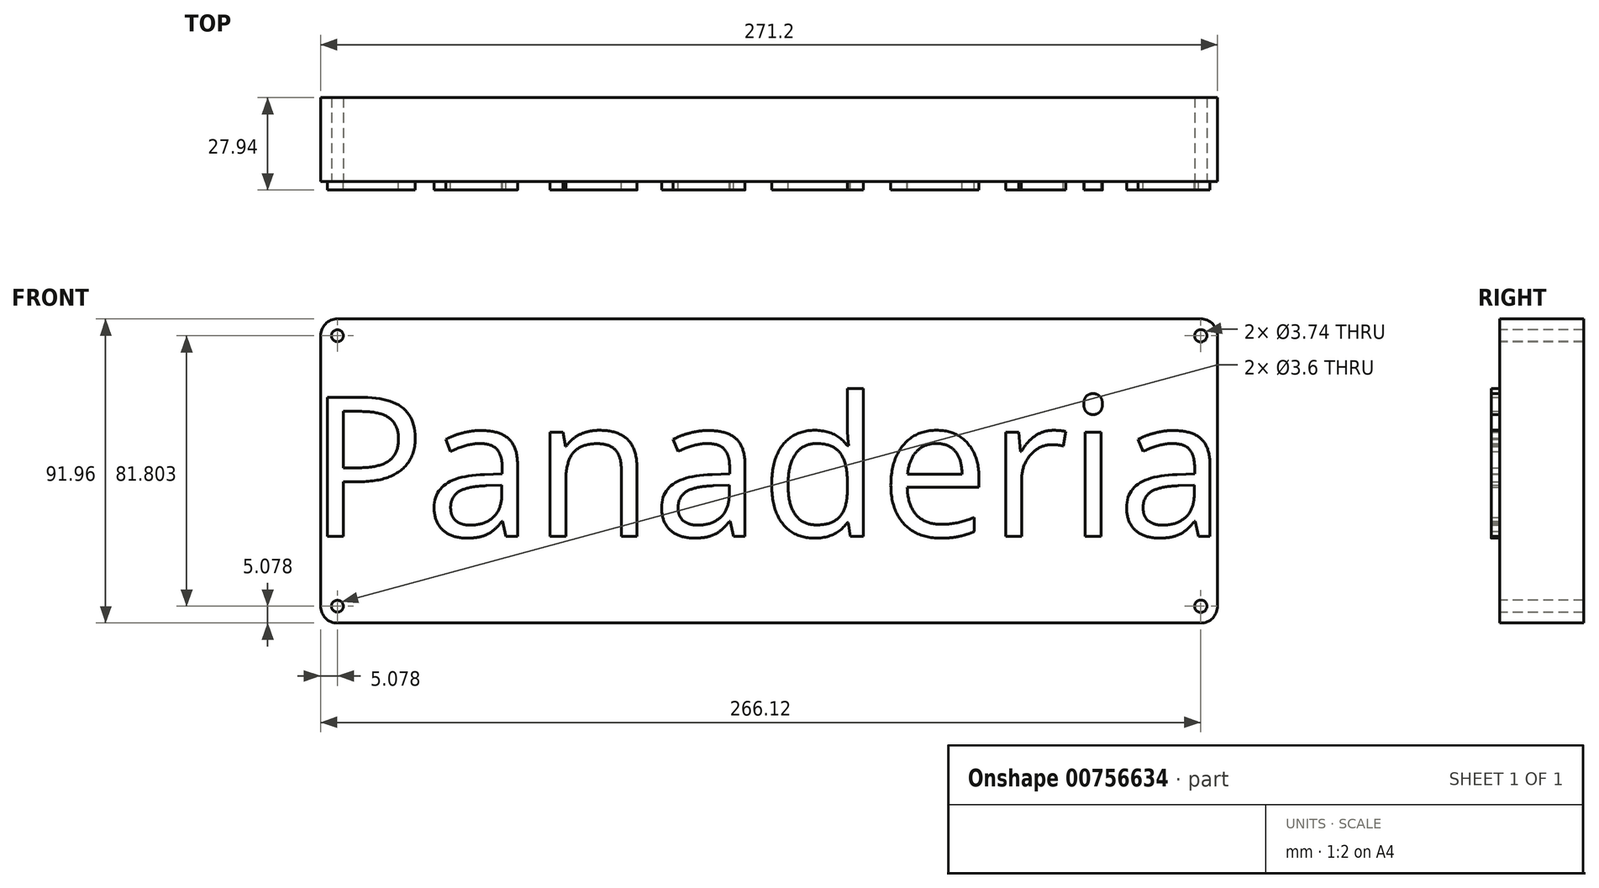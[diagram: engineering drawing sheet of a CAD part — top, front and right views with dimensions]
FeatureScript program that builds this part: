
annotation { "Feature Type Name" : "Feature", "Feature Type Description" : "" }
export const myFeature = defineFeature(function(context is Context, id is Id, definition is map)
    precondition{}
    {
        {
            var Q0;
            Q0=qCreatedBy(makeId("Front.planeOp"),FACE);
            var sketch = newSketch(context, id + "F0", { "sketchPlane" : qUnion([Q0])});
            skLineSegment(sketch, "E0.bottom", {"start": v(138.64, -45.98) * mm, "end": v(-132.56, -45.98) * mm});
            skLineSegment(sketch, "E0.top", {"start": v(138.64, 45.98) * mm, "end": v(-132.56, 45.98) * mm});
            skLineSegment(sketch, "E0.left", {"start": v(138.64, -45.98) * mm, "end": v(138.64, 45.98) * mm});
            skLineSegment(sketch, "E0.right", {"start": v(-132.56, -45.98) * mm, "end": v(-132.56, 45.98) * mm});
            skPoint(sketch, "E0.middle", {"position": v(3.04, 0) * mm});
            skSolve(sketch);
        }
        {
            var Q0;
            Q0=makeQuery(id+"F0.imprint","IMPRINT",FACE,{"disambiguationData":[TD([[makeQuery(id+"F0.imprint","IMPRINT",EDGE,{"derivedFrom":sQuery(id+"F0.wireOp",EDGE,"E0.bottom")}),-1.0]])]});
            extrude(context, id + "F1", {"entities" : qUnion([Q0]), "surfaceOperationType" : NewSurfaceOperationType.ADD, "depth" : 25.4 * mm, "offsetDistance" : 25.4 * mm});
        }
        {
            var Q0;
            Q0=makeQuery(id+"F1.opExtrude","CAP_FACE",FACE,{"disambiguationData":[OSD([sQuery(id+"F0.wireOp",EDGE,"E0.bottom"),sQuery(id+"F0.wireOp",EDGE,"E0.top"),sQuery(id+"F0.wireOp",EDGE,"E0.left"),sQuery(id+"F0.wireOp",EDGE,"E0.right")])],"isStart":false});
            var sketch = newSketch(context, id + "F2", { "sketchPlane" : qUnion([Q0])});
            skText(sketch, "E1", { "text": "Panaderia", "fontName": "OpenSans-Regular.ttf"});
            const initialGuessF2  = {"E1": [-0.13633, -0.01973, 1, 0, 0.04233]};
            skSetInitialGuess(sketch, initialGuessF2);
            skSolve(sketch);
        }
        {
            var Q0;
            Q0 = qSketchRegion(id + "F2", true);
            extrude(context, id + "F3", {"entities" : qUnion([Q0]), "operationType" : NewBodyOperationType.ADD, "depth" : 2.54 * mm, "offsetDistance" : 25.4 * mm});
        }
        {
            var Q0;
            Q0=makeQuery(id+"F1.opExtrude","SWEPT_EDGE",EDGE,{"disambiguationData":[OSD([sQuery(id+"F0.wireOp",EDGE,"E0.top"),sQuery(id+"F0.wireOp",EDGE,"E0.left")])]});
            fillet(context, id + "F4", {"entities" : qUnion([Q0]), "radius" : 5.08 * mm, "tangentPropagation" : true, "allowEdgeOverflow" : false});
        }
        {
            var Q0;
            Q0=makeQuery(id+"F1.opExtrude","SWEPT_EDGE",EDGE,{"disambiguationData":[OSD([sQuery(id+"F0.wireOp",EDGE,"E0.bottom"),sQuery(id+"F0.wireOp",EDGE,"E0.left")])]});
            fillet(context, id + "F5", {"entities" : qUnion([Q0]), "radius" : 5.08 * mm, "tangentPropagation" : true, "allowEdgeOverflow" : false});
        }
        {
            var Q0;
            Q0=makeQuery(id+"F1.opExtrude","SWEPT_EDGE",EDGE,{"disambiguationData":[OSD([sQuery(id+"F0.wireOp",EDGE,"E0.top"),sQuery(id+"F0.wireOp",EDGE,"E0.right")])]});
            var Q1;
            Q1=makeQuery(id+"F1.opExtrude","SWEPT_EDGE",EDGE,{"disambiguationData":[OSD([sQuery(id+"F0.wireOp",EDGE,"E0.bottom"),sQuery(id+"F0.wireOp",EDGE,"E0.right")])]});
            fillet(context, id + "F6", {"entities" : qUnion([Q0, Q1]), "radius" : 5.08 * mm, "tangentPropagation" : true, "allowEdgeOverflow" : false});
        }
        {
            var Q0;
            {var subQ0=sQuery(id+"F0.wireOp",EDGE,"E0.top");var subQ1=sQuery(id+"F0.wireOp",EDGE,"E0.right");var subQ2=sQuery(id+"F0.wireOp",EDGE,"E0.bottom");var subQ3=sQuery(id+"F0.wireOp",EDGE,"E0.left");Q0=makeQuery(id+"F3.boolean.opBoolean","SPLIT",FACE,{"disambiguationData":[TD([makeQuery(id+"F1.opExtrude","SWEPT_FACE",FACE,{"disambiguationData":[OSD([subQ2])]})])],"derivedFrom":makeQuery(id+"F1.opExtrude","CAP_FACE",FACE,{"disambiguationData":[OSD([subQ2,subQ0,subQ3,subQ1])],"isStart":false})});}
            var sketch = newSketch(context, id + "F7", { "sketchPlane" : qUnion([Q0])});
            skCircle(sketch, "E2", {"center": v(-127.48, 40.9) * mm, "radius": 1.8 * mm});
            skCircle(sketch, "E3", {"center": v(-127.48, -40.9) * mm, "radius": 1.8 * mm});
            skCircle(sketch, "E4", {"center": v(133.56, -40.9) * mm, "radius": 1.87 * mm});
            skCircle(sketch, "E5", {"center": v(133.56, 40.9) * mm, "radius": 1.87 * mm});
            skSolve(sketch);
        }
        {
            var Q0;
            Q0=makeQuery(id+"F7.imprint","IMPRINT",FACE,{"disambiguationData":[TD([[makeQuery(id+"F7.imprint","IMPRINT",EDGE,{"derivedFrom":sQuery(id+"F7.wireOp",EDGE,"E5")}),1.0]])]});
            var Q1;
            Q1=makeQuery(id+"F7.imprint","IMPRINT",FACE,{"disambiguationData":[TD([[makeQuery(id+"F7.imprint","IMPRINT",EDGE,{"derivedFrom":sQuery(id+"F7.wireOp",EDGE,"E4")}),1.0]])]});
            var Q2;
            Q2=makeQuery(id+"F7.imprint","IMPRINT",FACE,{"disambiguationData":[TD([[makeQuery(id+"F7.imprint","IMPRINT",EDGE,{"derivedFrom":sQuery(id+"F7.wireOp",EDGE,"E3")}),1.0]])]});
            var Q3;
            Q3=makeQuery(id+"F7.imprint","IMPRINT",FACE,{"disambiguationData":[TD([[makeQuery(id+"F7.imprint","IMPRINT",EDGE,{"derivedFrom":sQuery(id+"F7.wireOp",EDGE,"E2")}),1.0]])]});
            extrude(context, id + "F8", {"entities" : qUnion([Q0, Q1, Q2, Q3]), "operationType" : NewBodyOperationType.REMOVE, "oppositeDirection" : true, "depth" : 36.83 * mm, "offsetDistance" : 25.4 * mm});
        }
    });
